# Revit family: Hager-Univers-IP30-syst-Saillie-CH-fr
name_source: partatom
category: Electrical Equipment
units: mm (PartAtom-declared; Revit-internal decimal feet)

## family parameters
Cut with Voids When Loaded = No
Host = Face
Panel Configuration = Two Columns, Circuits Across
Part Type = Panelboard
Room Calculation Point = No
Round Connector Dimension = Use Diameter
Shared = No

## types (20) — shared parameters
EF000003 - mode de pose = EV000384 - saillie
EF000007 - couleur = EV000202 - blanc
EF000049 - profondeur = 161 mm  [stored 0.528215 ft]
EF000116 - numéro RAL = 9010
EF000118 - avec cadre/support de montage = No
EF000339 - type de capot = EV000494 - sans
EF001062 - finition CEM = No
EF001088 - possibilité de montage en saillie = Yes
EF001131 - profondeur intérieure = 161 mm  [stored 0.528215 ft]
EF001134 - rail DIN = Yes
EF001596 - matériau du boîtier/corps = EV000179 - acier
EF002950 - largeur en nombre de modules = 12
EF004462 - type de fermeture = EV000154 - autre
EF005474 - indice de protection (IP) = EV006410 - IP30
EF006244 - couvercle/porte transparent(e) = No
EF006306 - avec serrure = No
EF009212 - finition du couvercle = EV009916 - avec échancrure
EF015776 - borne de mise à la terre = Yes
EF015777 - borne à conducteur neutre = Yes
EF015941 - porte pour transmission du signal = No
HG000002 - avec porte = No
HG000003 - Gamme = Univers
HG000005 - Epaisseur = 3 mm  [stored 0.00984252 ft]
HG000006 - Encastré = No
HG000009 - Porte à double battant = No
HG000010 - Portes asymétriques = No
HG000011 - Rangées du bas vides = No
HG000017 - Distance entre pôles = 18 mm  [stored 0.0590551 ft]
Manufacturer = Hager
Type Comments = Univers
zero-valued in all types: Default Elevation, EF000218 - profondeur d'encastrement, EF000332 - hauteur d'encastrement, EF000846 - largeur d'encastrement, HG000007 - Nombre de colonnes vides, HG000008 - Nombre de rangées vides

## per-type parameters (varying)
| type | EF000008 - largeur | EF000040 - hauteur | EF000266 - nombre de rangées | HG000001 - nombre de colonnes | HG000004 - Référence fabricant | Model |
| Saillie IP30 L1050 H1100 P161 12 Modules - FWB74T1S | 1050 mm | 1100 mm | 28 | 4 | FWB74T1S | FWB74T1S |
| Saillie IP30 L1050 H500 P161 12 Modules - FWB34T1S | 1050 mm | 500 mm  [stored 1.64042 ft] | 12 | 4 | FWB34T1S | FWB34T1S |
| Saillie IP30 L1050 H650 P161 12 Modules - FWB44T1S | 1050 mm | 650 mm  [stored 2.13255 ft] | 16 | 4 | FWB44T1S | FWB44T1S |
| Saillie IP30 L1050 H800 P161 12 Modules - FWB54T1S | 1050 mm | 800 mm  [stored 2.62467 ft] | 20 | 4 | FWB54T1S | FWB54T1S |
| Saillie IP30 L1050 H950 P161 12 Modules - FWB64T1S | 1050 mm | 950 mm  [stored 3.1168 ft] | 24 | 4 | FWB64T1S | FWB64T1S |
| Saillie IP30 L300 H1100 P161 12 Modules - FWB71T1S | 300 mm | 1100 mm | 7 | 1 | FWB71T1S | FWB71T1S |
| Saillie IP30 L300 H500 P161 12 Modules - FWB31T1S | 300 mm | 500 mm  [stored 1.64042 ft] | 3 | 1 | FWB31T1S | FWB31T1S |
| Saillie IP30 L300 H650 P161 12 Modules - FWB41T1S | 300 mm | 650 mm  [stored 2.13255 ft] | 4 | 1 | FWB41T1S | FWB41T1S |
| Saillie IP30 L300 H800 P161 12 Modules - FWB51T1S | 300 mm | 800 mm  [stored 2.62467 ft] | 5 | 1 | FWB51T1S | FWB51T1S |
| Saillie IP30 L300 H950 P161 12 Modules - FWB61T1S | 300 mm | 950 mm  [stored 3.1168 ft] | 6 | 1 | FWB61T1S | FWB61T1S |
| Saillie IP30 L550 H1100 P161 12 Modules - FWB72T1S | 550 mm | 1100 mm | 14 | 2 | FWB72T1S | FWB72T1S |
| Saillie IP30 L550 H500 P161 12 Modules - FWB32T1S | 550 mm | 500 mm  [stored 1.64042 ft] | 6 | 2 | FWB32T1S | FWB32T1S |
| Saillie IP30 L550 H650 P161 12 Modules - FWB42T1S | 550 mm | 650 mm  [stored 2.13255 ft] | 8 | 2 | FWB42T1S | FWB42T1S |
| Saillie IP30 L550 H800 P161 12 Modules - FWB52T1S | 550 mm | 800 mm  [stored 2.62467 ft] | 10 | 2 | FWB52T1S | FWB52T1S |
| Saillie IP30 L550 H950 P161 12 Modules - FWB62T1S | 550 mm | 950 mm  [stored 3.1168 ft] | 12 | 2 | FWB62T1S | FWB62T1S |
| Saillie IP30 L800 H1100 P161 12 Modules - FWB73T1S | 800 mm  [stored 2.62467 ft] | 1100 mm | 21 | 3 | FWB73T1S | FWB73T1S |
| Saillie IP30 L800 H500 P161 12 Modules - FWB33T1S | 800 mm  [stored 2.62467 ft] | 500 mm  [stored 1.64042 ft] | 9 | 3 | FWB33T1S | FWB33T1S |
| Saillie IP30 L800 H650 P161 12 Modules - FWB43T1S | 800 mm  [stored 2.62467 ft] | 650 mm  [stored 2.13255 ft] | 12 | 3 | FWB43T1S | FWB43T1S |
| Saillie IP30 L800 H800 P161 12 Modules - FWB53T1S | 800 mm  [stored 2.62467 ft] | 800 mm  [stored 2.62467 ft] | 15 | 3 | FWB53T1S | FWB53T1S |
| Saillie IP30 L800 H950 P161 12 Modules - FWB63T1S | 800 mm  [stored 2.62467 ft] | 950 mm  [stored 3.1168 ft] | 18 | 3 | FWB63T1S | FWB63T1S |

note: [stored X ft] marks values corroborated as IEEE doubles in the binary element streams (Revit-internal decimal feet)

## geometry (parser evidence)
native form markers: Sweep x17
no freeform markers — native parametric forms only
